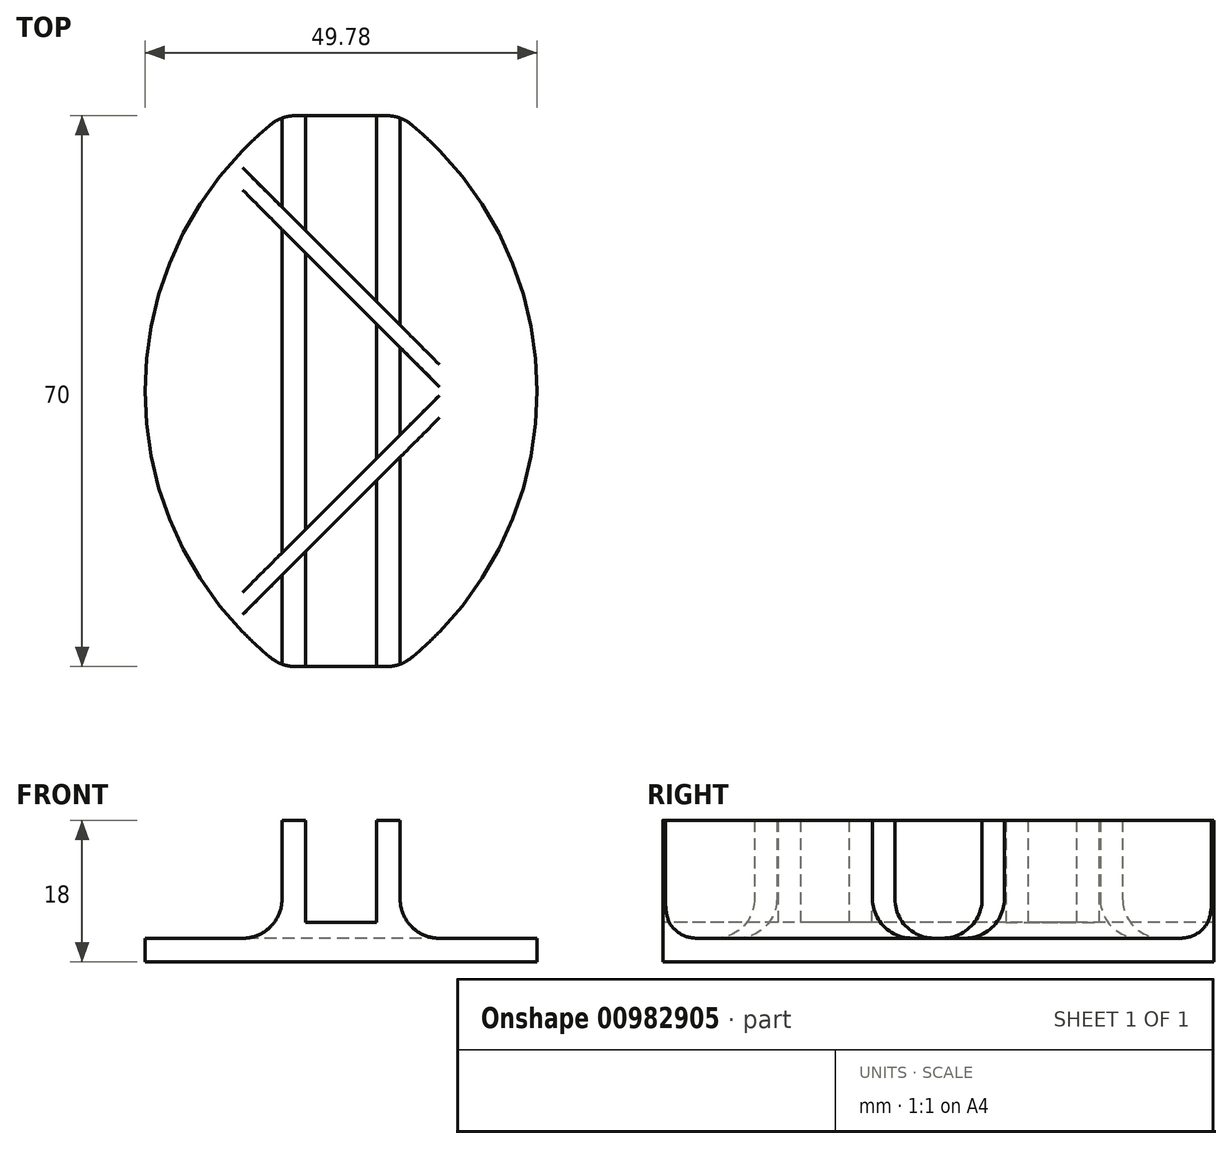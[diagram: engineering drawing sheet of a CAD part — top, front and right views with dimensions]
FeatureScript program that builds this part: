
annotation { "Feature Type Name" : "Feature", "Feature Type Description" : "" }
export const myFeature = defineFeature(function(context is Context, id is Id, definition is map)
    precondition{}
    {
        {
            var Q0;
            Q0=qCreatedBy(makeId("Top.planeOp"),FACE);
            var sketch = newSketch(context, id + "F0", { "sketchPlane" : qUnion([Q0])});
            skLineSegment(sketch, "E0.bottom", {"start": v(4.5, -35) * mm, "end": v(-4.5, -35) * mm});
            skLineSegment(sketch, "E0.top", {"start": v(4.5, 35) * mm, "end": v(-4.5, 35) * mm});
            skLineSegment(sketch, "E0.left", {"start": v(4.5, -35) * mm, "end": v(4.5, 35) * mm});
            skLineSegment(sketch, "E0.right", {"start": v(-4.5, -35) * mm, "end": v(-4.5, 35) * mm});
            skPoint(sketch, "E0.middle", {"position": v(0, 0) * mm});
            skLineSegment(sketch, "E1.0", {"start": v(7.5, -35) * mm, "end": v(7.5, 35) * mm});
            skLineSegment(sketch, "E2.0", {"start": v(-7.5, -35) * mm, "end": v(-7.5, 35) * mm});
            skLineSegment(sketch, "E3", {"start": v(-7.5, 35) * mm, "end": v(7.5, 35) * mm});
            skLineSegment(sketch, "E4", {"start": v(-7.5, -35) * mm, "end": v(7.5, -35) * mm});
            skSolve(sketch);
        }
        {
            var Q0;
            {var subQ0=sQuery(id+"F0.wireOp",EDGE,"E0.right");Q0=makeQuery(id+"F0.imprint","IMPRINT",FACE,{"disambiguationData":[TD([[makeQuery(id+"F0.imprint","IMPRINT",EDGE,{"derivedFrom":subQ0}),1.0]])]});}
            var Q1;
            {var subQ0=sQuery(id+"F0.wireOp",EDGE,"E0.left");Q1=makeQuery(id+"F0.imprint","IMPRINT",FACE,{"disambiguationData":[TD([[makeQuery(id+"F0.imprint","IMPRINT",EDGE,{"derivedFrom":subQ0}),1.0]])]});}
            var Q2;
            {var subQ0=sQuery(id+"F0.wireOp",EDGE,"E0.left");Q2=makeQuery(id+"F0.imprint","IMPRINT",FACE,{"disambiguationData":[TD([[makeQuery(id+"F0.imprint","IMPRINT",EDGE,{"derivedFrom":subQ0}),-1.0]])]});}
            extrude(context, id + "F1", {"entities" : qUnion([Q0, Q1, Q2]), "depth" : 5 * mm, "offsetDistance" : 25 * mm});
        }
        {
            var Q0;
            {var subQ0=sQuery(id+"F0.wireOp",EDGE,"E0.right");Q0=makeQuery(id+"F0.imprint","IMPRINT",FACE,{"disambiguationData":[TD([[makeQuery(id+"F0.imprint","IMPRINT",EDGE,{"derivedFrom":subQ0}),1.0]])]});}
            var Q1;
            {var subQ0=sQuery(id+"F0.wireOp",EDGE,"E0.left");Q1=makeQuery(id+"F0.imprint","IMPRINT",FACE,{"disambiguationData":[TD([[makeQuery(id+"F0.imprint","IMPRINT",EDGE,{"derivedFrom":subQ0}),-1.0]])]});}
            extrude(context, id + "F2", {"entities" : qUnion([Q0, Q1]), "operationType" : NewBodyOperationType.ADD, "depth" : 18 * mm, "offsetDistance" : 25 * mm});
        }
        {
            var Q0;
            Q0=makeQuery(id+"F1.opExtrude","CAP_FACE",FACE,{"disambiguationData":[OSD([sQuery(id+"F0.wireOp",EDGE,"E1.0"),sQuery(id+"F0.wireOp",EDGE,"E2.0"),sQuery(id+"F0.wireOp",EDGE,"E3"),sQuery(id+"F0.wireOp",EDGE,"E4")])],"isStart":true});
            var sketch = newSketch(context, id + "F3", { "sketchPlane" : qUnion([Q0])});
            skArc(sketch, "E5", {"start": v(-7.5, 35) * mm, "mid": v(-24.89, 0) * mm, "end": v(-7.5, -35) * mm});
            skLineSegment(sketch, "E6", {"start": v(0, -17) * mm, "end": v(0, 21.24) * mm, "construction": true});
            skArc(sketch, "E7.MirrorCS", {"start": v(7.5, 35) * mm, "mid": v(24.89, 0) * mm, "end": v(7.5, -35) * mm});
            skLineSegment(sketch, "E8.0", {"start": v(-7.5, -35) * mm, "end": v(7.5, -35) * mm});
            skLineSegment(sketch, "E9.0", {"start": v(-7.5, 35) * mm, "end": v(7.5, 35) * mm});
            skSolve(sketch);
        }
        {
            var Q0;
            Q0 = qSketchRegion(id + "F3", true);
            extrude(context, id + "F4", {"entities" : qUnion([Q0]), "operationType" : NewBodyOperationType.ADD, "oppositeDirection" : true, "depth" : 3 * mm, "offsetDistance" : 25 * mm});
        }
        {
            var Q0;
            {var subQ0=sQuery(id+"F0.wireOp",EDGE,"E1.0");var subQ1=sQuery(id+"F0.wireOp",EDGE,"E3");Q0=makeQuery(id+"F4.boolean.opBoolean","MERGE",EDGE,{"derivedFrom":[makeQuery(id+"F2.boolean.opBoolean","MERGE",EDGE,{"derivedFrom":[makeQuery(id+"F1.opExtrude","SWEPT_EDGE",EDGE,{"disambiguationData":[OSD([subQ0,subQ1])]}),makeQuery(id+"F2.opExtrude","SWEPT_EDGE",EDGE,{"disambiguationData":[OSD([subQ0,subQ1])]})]}),makeQuery(id+"F4.opExtrude","SWEPT_EDGE",EDGE,{"disambiguationData":[OSD([subQ0,sQuery(id+"F3.wireOp",EDGE,"E7.MirrorCS"),sQuery(id+"F3.wireOp",EDGE,"E8.0")])]})]});}
            var Q1;
            {var subQ0=sQuery(id+"F0.wireOp",EDGE,"E2.0");var subQ1=sQuery(id+"F0.wireOp",EDGE,"E3");Q1=makeQuery(id+"F4.boolean.opBoolean","MERGE",EDGE,{"derivedFrom":[makeQuery(id+"F2.boolean.opBoolean","MERGE",EDGE,{"derivedFrom":[makeQuery(id+"F1.opExtrude","SWEPT_EDGE",EDGE,{"disambiguationData":[OSD([subQ0,subQ1])]}),makeQuery(id+"F2.opExtrude","SWEPT_EDGE",EDGE,{"disambiguationData":[OSD([subQ0,subQ1])]})]}),makeQuery(id+"F4.opExtrude","SWEPT_EDGE",EDGE,{"disambiguationData":[OSD([subQ0,sQuery(id+"F3.wireOp",EDGE,"E5"),sQuery(id+"F3.wireOp",EDGE,"E8.0")])]})]});}
            var Q2;
            {var subQ0=sQuery(id+"F0.wireOp",EDGE,"E1.0");var subQ1=sQuery(id+"F0.wireOp",EDGE,"E4");Q2=makeQuery(id+"F4.boolean.opBoolean","MERGE",EDGE,{"derivedFrom":[makeQuery(id+"F2.boolean.opBoolean","MERGE",EDGE,{"derivedFrom":[makeQuery(id+"F1.opExtrude","SWEPT_EDGE",EDGE,{"disambiguationData":[OSD([subQ0,subQ1])]}),makeQuery(id+"F2.opExtrude","SWEPT_EDGE",EDGE,{"disambiguationData":[OSD([subQ0,subQ1])]})]}),makeQuery(id+"F4.opExtrude","SWEPT_EDGE",EDGE,{"disambiguationData":[OSD([subQ0,sQuery(id+"F3.wireOp",EDGE,"E7.MirrorCS"),sQuery(id+"F3.wireOp",EDGE,"E9.0")])]})]});}
            var Q3;
            {var subQ0=sQuery(id+"F0.wireOp",EDGE,"E2.0");var subQ1=sQuery(id+"F0.wireOp",EDGE,"E4");Q3=makeQuery(id+"F4.boolean.opBoolean","MERGE",EDGE,{"derivedFrom":[makeQuery(id+"F2.boolean.opBoolean","MERGE",EDGE,{"derivedFrom":[makeQuery(id+"F1.opExtrude","SWEPT_EDGE",EDGE,{"disambiguationData":[OSD([subQ0,subQ1])]}),makeQuery(id+"F2.opExtrude","SWEPT_EDGE",EDGE,{"disambiguationData":[OSD([subQ0,subQ1])]})]}),makeQuery(id+"F4.opExtrude","SWEPT_EDGE",EDGE,{"disambiguationData":[OSD([subQ0,sQuery(id+"F3.wireOp",EDGE,"E5"),sQuery(id+"F3.wireOp",EDGE,"E9.0")])]})]});}
            fillet(context, id + "F5", {"entities" : qUnion([Q0, Q1, Q2, Q3]), "radius" : 5 * mm, "allowEdgeOverflow" : false});
        }
        {
            var Q0;
            Q0=makeQuery(id+"F2.opExtrude","CAP_FACE",FACE,{"disambiguationData":[OSD([sQuery(id+"F0.wireOp",EDGE,"E0.right"),sQuery(id+"F0.wireOp",EDGE,"E2.0"),sQuery(id+"F0.wireOp",EDGE,"E3"),sQuery(id+"F0.wireOp",EDGE,"E4")])],"isStart":false});
            var sketch = newSketch(context, id + "F6", { "sketchPlane" : qUnion([Q0])});
            skLineSegment(sketch, "E10", {"start": v(39.73, 23.85) * mm, "end": v(-30.72, -46.6) * mm});
            skLineSegment(sketch, "E11.0", {"start": v(-7.5, -34.69) * mm, "end": v(-7.5, 34.69) * mm, "construction": true});
            skLineSegment(sketch, "E12.0", {"start": v(38.31, 25.27) * mm, "end": v(-32.13, -45.18) * mm});
            skLineSegment(sketch, "E13", {"start": v(39.73, 23.85) * mm, "end": v(38.31, 25.27) * mm});
            skLineSegment(sketch, "E14", {"start": v(-30.72, -46.6) * mm, "end": v(-32.13, -45.18) * mm});
            skLineSegment(sketch, "E15", {"start": v(45.67, -29.8) * mm, "end": v(-38.01, 53.89) * mm});
            skLineSegment(sketch, "E16.0", {"start": v(44.26, -31.21) * mm, "end": v(-39.43, 52.47) * mm});
            skLineSegment(sketch, "E17", {"start": v(-39.43, 52.47) * mm, "end": v(-38.01, 53.89) * mm});
            skLineSegment(sketch, "E18", {"start": v(44.26, -31.21) * mm, "end": v(45.67, -29.8) * mm});
            skSolve(sketch);
        }
        {
            var Q0;
            Q0 = qSketchRegion(id + "F6", true);
            var Q1;
            {var subQ0=sQuery(id+"F0.wireOp",EDGE,"E1.0");var subQ6=sQuery(id+"F3.wireOp",EDGE,"E7.MirrorCS");Q1=makeQuery(id+"F4.boolean.opBoolean","SPLIT",FACE,{"disambiguationData":[TD([makeQuery(id+"F1.opExtrude","SWEPT_FACE",FACE,{"disambiguationData":[OSD([subQ0])]})])],"derivedFrom":makeQuery(id+"F4.opExtrude","CAP_FACE",FACE,{"disambiguationData":[OSD([sQuery(id+"F3.wireOp",EDGE,"E5"),subQ6,sQuery(id+"F3.wireOp",EDGE,"E8.0"),sQuery(id+"F3.wireOp",EDGE,"E9.0")])],"isStart":false})});}
            extrude(context, id + "F7", {"entities" : qUnion([Q0]), "operationType" : NewBodyOperationType.REMOVE, "endBound" : BoundingType.UP_TO_SURFACE, "oppositeDirection" : true, "depth" : 25 * mm, "endBoundEntityFace" : qUnion([Q1]), "offsetDistance" : 25 * mm});
        }
        {
            var Q0;
            {var subQ0=sQuery(id+"F3.wireOp",EDGE,"E8.0");var subQ1=sQuery(id+"F3.wireOp",EDGE,"E5");var subQ2=sQuery(id+"F0.wireOp",EDGE,"E2.0");var subQ6=makeQuery(id+"F4.opExtrude","CAP_FACE",FACE,{"disambiguationData":[OSD([subQ1,sQuery(id+"F3.wireOp",EDGE,"E7.MirrorCS"),subQ0,sQuery(id+"F3.wireOp",EDGE,"E9.0")])],"isStart":false});var subQ7=makeQuery(id+"F2.opExtrude","SWEPT_FACE",FACE,{"disambiguationData":[OSD([subQ2])]});var subQ8=makeQuery(id+"F1.opExtrude","SWEPT_FACE",FACE,{"disambiguationData":[OSD([subQ2])]});Q0=makeQuery(id+"F7.boolean.opBoolean","SPLIT",EDGE,{"disambiguationData":[TD([makeQuery(id+"F5.opFillet","BLEND_FACE",FACE,{"disambiguationData":[OSD([subQ2,sQuery(id+"F0.wireOp",EDGE,"E3"),subQ1,subQ0])]})])],"derivedFrom":makeQuery(id+"F4.boolean.opBoolean","INTERSECT",EDGE,{"derivedFrom":[makeQuery(id+"F2.boolean.opBoolean","MERGE",FACE,{"derivedFrom":[subQ8,subQ7]}),subQ6]})});}
            var Q1;
            {var subQ1=sQuery(id+"F6.wireOp",EDGE,"E16.0");var subQ2=sQuery(id+"F6.wireOp",EDGE,"E14");var subQ3=sQuery(id+"F6.wireOp",EDGE,"E12.0");var subQ4=makeQuery(id+"F4.opExtrude","CAP_FACE",FACE,{"disambiguationData":[OSD([sQuery(id+"F3.wireOp",EDGE,"E5"),sQuery(id+"F3.wireOp",EDGE,"E7.MirrorCS"),sQuery(id+"F3.wireOp",EDGE,"E8.0"),sQuery(id+"F3.wireOp",EDGE,"E9.0")])],"isStart":false});var subQ5=sQuery(id+"F0.wireOp",EDGE,"E2.0");var subQ6=makeQuery(id+"F2.opExtrude","SWEPT_FACE",FACE,{"disambiguationData":[OSD([subQ5])]});var subQ7=makeQuery(id+"F1.opExtrude","SWEPT_FACE",FACE,{"disambiguationData":[OSD([subQ5])]});var subQ8=makeQuery(id+"F2.opExtrude","CAP_EDGE",EDGE,{"disambiguationData":[OSD([subQ5])],"isStart":false});var subQ9=makeQuery(id+"F6.imprint","INTERSECT",VERTEX,{"derivedFrom":[subQ8,subQ3]});var subQ12=makeQuery(id+"F6.imprint","INTERSECT",VERTEX,{"derivedFrom":[subQ3,subQ1]});Q1=makeQuery(id+"F7.boolean.opBoolean","SPLIT",EDGE,{"disambiguationData":[TD([makeQuery(id+"F7.opExtrude","SWEPT_FACE",FACE,{"disambiguationData":[OSD([subQ3]),TDD([makeQuery(id+"F6.imprint","IMPRINT",EDGE,{"disambiguationData":[TD([[subQ12,-1.0]])],"derivedFrom":subQ3}),makeQuery(id+"F6.imprint","IMPRINT",EDGE,{"disambiguationData":[TD([[subQ9,1.0]])],"derivedFrom":subQ3}),makeQuery(id+"F6.imprint","IMPRINT",EDGE,{"disambiguationData":[TD([[makeQuery(id+"F6.imprint","INTERSECT",VERTEX,{"derivedFrom":[subQ3,subQ2]}),1.0]])],"derivedFrom":subQ3})])]})])],"derivedFrom":makeQuery(id+"F4.boolean.opBoolean","INTERSECT",EDGE,{"derivedFrom":[makeQuery(id+"F2.boolean.opBoolean","MERGE",FACE,{"derivedFrom":[subQ7,subQ6]}),subQ4]})});}
            var Q2;
            {var subQ0=sQuery(id+"F3.wireOp",EDGE,"E9.0");var subQ1=sQuery(id+"F3.wireOp",EDGE,"E5");var subQ2=sQuery(id+"F0.wireOp",EDGE,"E2.0");var subQ3=makeQuery(id+"F4.opExtrude","CAP_FACE",FACE,{"disambiguationData":[OSD([subQ1,sQuery(id+"F3.wireOp",EDGE,"E7.MirrorCS"),sQuery(id+"F3.wireOp",EDGE,"E8.0"),subQ0])],"isStart":false});var subQ4=makeQuery(id+"F2.opExtrude","SWEPT_FACE",FACE,{"disambiguationData":[OSD([subQ2])]});var subQ5=makeQuery(id+"F1.opExtrude","SWEPT_FACE",FACE,{"disambiguationData":[OSD([subQ2])]});Q2=makeQuery(id+"F7.boolean.opBoolean","SPLIT",EDGE,{"disambiguationData":[TD([makeQuery(id+"F5.opFillet","BLEND_FACE",FACE,{"disambiguationData":[OSD([subQ2,sQuery(id+"F0.wireOp",EDGE,"E4"),subQ1,subQ0])]})])],"derivedFrom":makeQuery(id+"F4.boolean.opBoolean","INTERSECT",EDGE,{"derivedFrom":[makeQuery(id+"F2.boolean.opBoolean","MERGE",FACE,{"derivedFrom":[subQ5,subQ4]}),subQ3]})});}
            var Q3;
            {var subQ0=sQuery(id+"F3.wireOp",EDGE,"E9.0");var subQ1=sQuery(id+"F3.wireOp",EDGE,"E7.MirrorCS");var subQ2=sQuery(id+"F0.wireOp",EDGE,"E1.0");var subQ3=makeQuery(id+"F4.opExtrude","CAP_FACE",FACE,{"disambiguationData":[OSD([sQuery(id+"F3.wireOp",EDGE,"E5"),subQ1,sQuery(id+"F3.wireOp",EDGE,"E8.0"),subQ0])],"isStart":false});var subQ4=makeQuery(id+"F1.opExtrude","SWEPT_FACE",FACE,{"disambiguationData":[OSD([subQ2])]});var subQ5=makeQuery(id+"F2.opExtrude","SWEPT_FACE",FACE,{"disambiguationData":[OSD([subQ2])]});Q3=makeQuery(id+"F7.boolean.opBoolean","SPLIT",EDGE,{"disambiguationData":[TD([makeQuery(id+"F5.opFillet","BLEND_FACE",FACE,{"disambiguationData":[OSD([subQ2,sQuery(id+"F0.wireOp",EDGE,"E4"),subQ1,subQ0])]})])],"derivedFrom":makeQuery(id+"F4.boolean.opBoolean","INTERSECT",EDGE,{"derivedFrom":[makeQuery(id+"F2.boolean.opBoolean","MERGE",FACE,{"derivedFrom":[subQ4,subQ5]}),subQ3]})});}
            var Q4;
            {var subQ1=sQuery(id+"F6.wireOp",EDGE,"E16.0");var subQ2=sQuery(id+"F6.wireOp",EDGE,"E14");var subQ3=sQuery(id+"F6.wireOp",EDGE,"E12.0");var subQ4=makeQuery(id+"F4.opExtrude","CAP_FACE",FACE,{"disambiguationData":[OSD([sQuery(id+"F3.wireOp",EDGE,"E5"),sQuery(id+"F3.wireOp",EDGE,"E7.MirrorCS"),sQuery(id+"F3.wireOp",EDGE,"E8.0"),sQuery(id+"F3.wireOp",EDGE,"E9.0")])],"isStart":false});var subQ5=sQuery(id+"F0.wireOp",EDGE,"E1.0");var subQ6=makeQuery(id+"F1.opExtrude","SWEPT_FACE",FACE,{"disambiguationData":[OSD([subQ5])]});var subQ7=makeQuery(id+"F2.opExtrude","SWEPT_FACE",FACE,{"disambiguationData":[OSD([subQ5])]});var subQ8=makeQuery(id+"F2.opExtrude","CAP_EDGE",EDGE,{"disambiguationData":[OSD([sQuery(id+"F0.wireOp",EDGE,"E2.0")])],"isStart":false});var subQ9=makeQuery(id+"F6.imprint","INTERSECT",VERTEX,{"derivedFrom":[subQ8,subQ3]});var subQ12=makeQuery(id+"F6.imprint","INTERSECT",VERTEX,{"derivedFrom":[subQ3,subQ1]});Q4=makeQuery(id+"F7.boolean.opBoolean","SPLIT",EDGE,{"disambiguationData":[TD([makeQuery(id+"F7.opExtrude","SWEPT_FACE",FACE,{"disambiguationData":[OSD([subQ3]),TDD([makeQuery(id+"F6.imprint","IMPRINT",EDGE,{"disambiguationData":[TD([[subQ12,-1.0]])],"derivedFrom":subQ3}),makeQuery(id+"F6.imprint","IMPRINT",EDGE,{"disambiguationData":[TD([[subQ9,1.0]])],"derivedFrom":subQ3}),makeQuery(id+"F6.imprint","IMPRINT",EDGE,{"disambiguationData":[TD([[makeQuery(id+"F6.imprint","INTERSECT",VERTEX,{"derivedFrom":[subQ3,subQ2]}),1.0]])],"derivedFrom":subQ3})])]})])],"derivedFrom":makeQuery(id+"F4.boolean.opBoolean","INTERSECT",EDGE,{"derivedFrom":[makeQuery(id+"F2.boolean.opBoolean","MERGE",FACE,{"derivedFrom":[subQ6,subQ7]}),subQ4]})});}
            var Q5;
            {var subQ0=sQuery(id+"F3.wireOp",EDGE,"E8.0");var subQ1=sQuery(id+"F3.wireOp",EDGE,"E7.MirrorCS");var subQ2=sQuery(id+"F0.wireOp",EDGE,"E1.0");var subQ3=makeQuery(id+"F4.opExtrude","CAP_FACE",FACE,{"disambiguationData":[OSD([sQuery(id+"F3.wireOp",EDGE,"E5"),subQ1,subQ0,sQuery(id+"F3.wireOp",EDGE,"E9.0")])],"isStart":false});var subQ4=makeQuery(id+"F1.opExtrude","SWEPT_FACE",FACE,{"disambiguationData":[OSD([subQ2])]});var subQ5=makeQuery(id+"F2.opExtrude","SWEPT_FACE",FACE,{"disambiguationData":[OSD([subQ2])]});Q5=makeQuery(id+"F7.boolean.opBoolean","SPLIT",EDGE,{"disambiguationData":[TD([makeQuery(id+"F5.opFillet","BLEND_FACE",FACE,{"disambiguationData":[OSD([subQ2,sQuery(id+"F0.wireOp",EDGE,"E3"),subQ1,subQ0])]})])],"derivedFrom":makeQuery(id+"F4.boolean.opBoolean","INTERSECT",EDGE,{"derivedFrom":[makeQuery(id+"F2.boolean.opBoolean","MERGE",FACE,{"derivedFrom":[subQ4,subQ5]}),subQ3]})});}
            fillet(context, id + "F8", {"entities" : qUnion([Q0, Q1, Q2, Q3, Q4, Q5]), "radius" : 5 * mm, "tangentPropagation" : true, "allowEdgeOverflow" : false});
        }
    });
